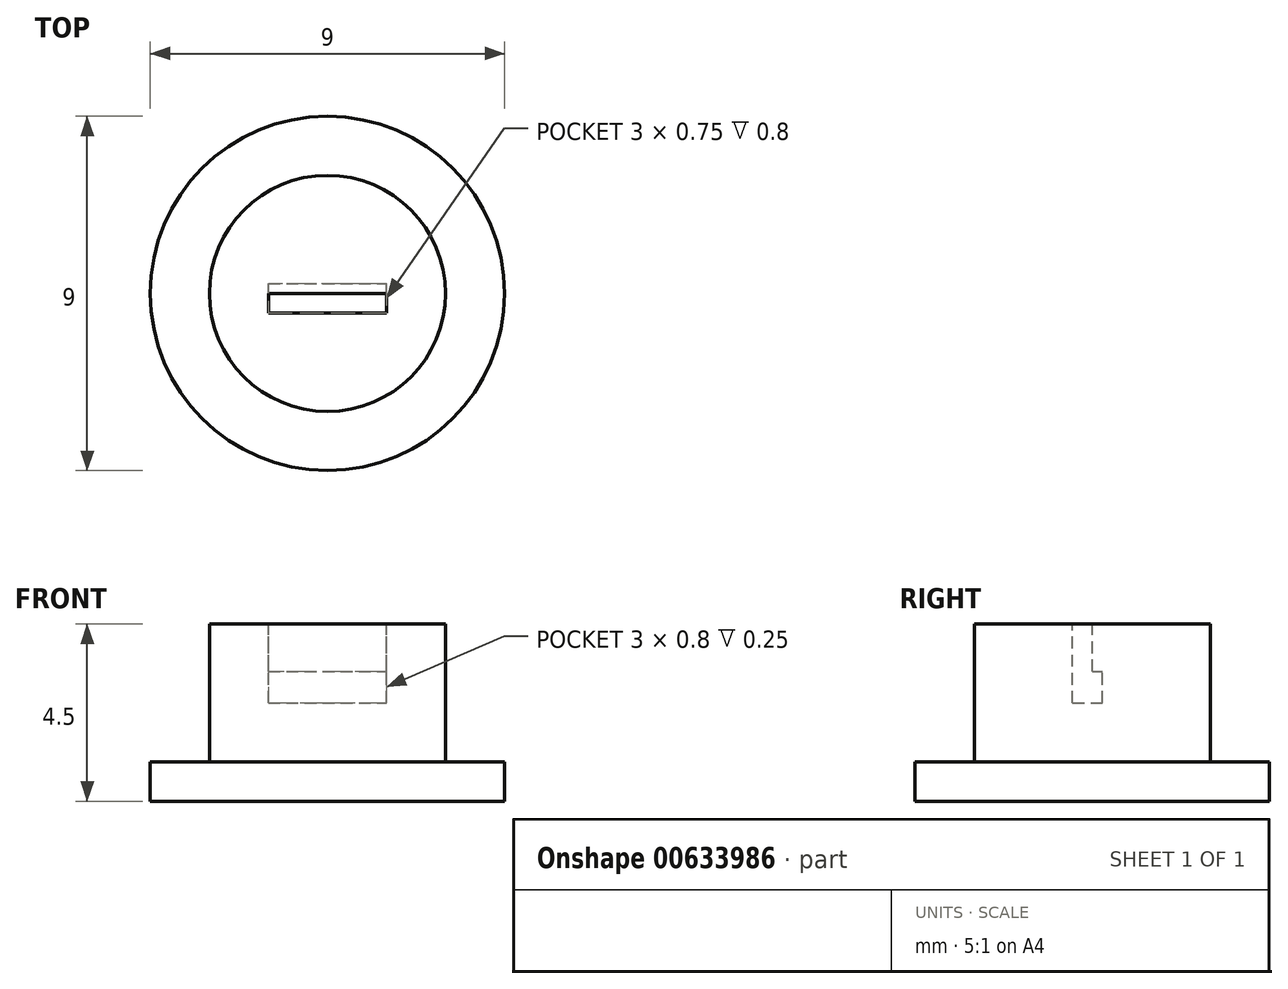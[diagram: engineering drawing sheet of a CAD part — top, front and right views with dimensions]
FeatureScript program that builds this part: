
annotation { "Feature Type Name" : "Feature", "Feature Type Description" : "" }
export const myFeature = defineFeature(function(context is Context, id is Id, definition is map)
    precondition{}
    {
        {
            var Q0;
            Q0=qCreatedBy(makeId("Top.planeOp"),FACE);
            var sketch = newSketch(context, id + "F0", { "sketchPlane" : qUnion([Q0])});
            skCircle(sketch, "E0", {"center": v(0, 0) * mm, "radius": 4.5 * mm});
            skSolve(sketch);
        }
        {
            var Q0;
            Q0=makeQuery(id+"F0.imprint","IMPRINT",FACE,{"disambiguationData":[TD([[makeQuery(id+"F0.imprint","IMPRINT",EDGE,{"derivedFrom":sQuery(id+"F0.wireOp",EDGE,"E0")}),1.0]])]});
            extrude(context, id + "F1", {"entities" : qUnion([Q0]), "depth" : 1 * mm, "offsetDistance" : 25.4 * mm});
        }
        {
            var Q0;
            Q0=makeQuery(id+"F1.opExtrude","CAP_FACE",FACE,{"disambiguationData":[OSD([sQuery(id+"F0.wireOp",EDGE,"E0")])],"isStart":false});
            var sketch = newSketch(context, id + "F2", { "sketchPlane" : qUnion([Q0])});
            skCircle(sketch, "E1", {"center": v(0, 0) * mm, "radius": 3 * mm});
            skSolve(sketch);
        }
        {
            var Q0;
            Q0=makeQuery(id+"F2.imprint","IMPRINT",FACE,{"disambiguationData":[TD([[makeQuery(id+"F2.imprint","IMPRINT",EDGE,{"derivedFrom":sQuery(id+"F2.wireOp",EDGE,"E1")}),1.0]])]});
            extrude(context, id + "F3", {"entities" : qUnion([Q0]), "operationType" : NewBodyOperationType.ADD, "depth" : 3.5 * mm, "offsetDistance" : 25.4 * mm});
        }
        {
            var Q0;
            Q0=makeQuery(id+"F3.opExtrude","CAP_FACE",FACE,{"disambiguationData":[OSD([sQuery(id+"F2.wireOp",EDGE,"E1")])],"isStart":false});
            var sketch = newSketch(context, id + "F4", { "sketchPlane" : qUnion([Q0])});
            skLineSegment(sketch, "E2.bottom", {"start": v(-1.5, -0.5) * mm, "end": v(1.5, -0.5) * mm});
            skLineSegment(sketch, "E2.top", {"start": v(-1.5, 0.25) * mm, "end": v(1.5, 0.25) * mm});
            skLineSegment(sketch, "E2.left", {"start": v(-1.5, -0.5) * mm, "end": v(-1.5, 0.25) * mm});
            skLineSegment(sketch, "E2.right", {"start": v(1.5, -0.5) * mm, "end": v(1.5, 0.25) * mm});
            skSolve(sketch);
        }
        {
            var Q0;
            Q0=makeQuery(id+"F4.imprint","IMPRINT",FACE,{"disambiguationData":[TD([[makeQuery(id+"F4.imprint","IMPRINT",EDGE,{"derivedFrom":sQuery(id+"F4.wireOp",EDGE,"E2.bottom")}),1.0]])]});
            extrude(context, id + "F5", {"entities" : qUnion([Q0]), "operationType" : NewBodyOperationType.REMOVE, "oppositeDirection" : true, "depth" : 2 * mm, "offsetDistance" : 25.4 * mm});
        }
        {
            var Q0;
            Q0=makeQuery(id+"F3.opExtrude","CAP_FACE",FACE,{"disambiguationData":[OSD([sQuery(id+"F2.wireOp",EDGE,"E1")])],"isStart":false});
            var sketch = newSketch(context, id + "F6", { "sketchPlane" : qUnion([Q0])});
            skLineSegment(sketch, "E3.bottom", {"start": v(1.5, 0) * mm, "end": v(-1.5, 0) * mm});
            skLineSegment(sketch, "E3.top", {"start": v(1.5, 0.25) * mm, "end": v(-1.5, 0.25) * mm});
            skLineSegment(sketch, "E3.left", {"start": v(1.5, 0) * mm, "end": v(1.5, 0.25) * mm});
            skLineSegment(sketch, "E3.right", {"start": v(-1.5, 0) * mm, "end": v(-1.5, 0.25) * mm});
            skSolve(sketch);
        }
        {
            var Q0;
            Q0=makeQuery(id+"F6.imprint","IMPRINT",FACE,{"disambiguationData":[TD([[makeQuery(id+"F6.imprint","IMPRINT",EDGE,{"derivedFrom":sQuery(id+"F6.wireOp",EDGE,"E3.bottom")}),-1.0]])]});
            extrude(context, id + "F7", {"entities" : qUnion([Q0]), "operationType" : NewBodyOperationType.ADD, "oppositeDirection" : true, "depth" : 1.2 * mm, "offsetDistance" : 25.4 * mm});
        }
    });
